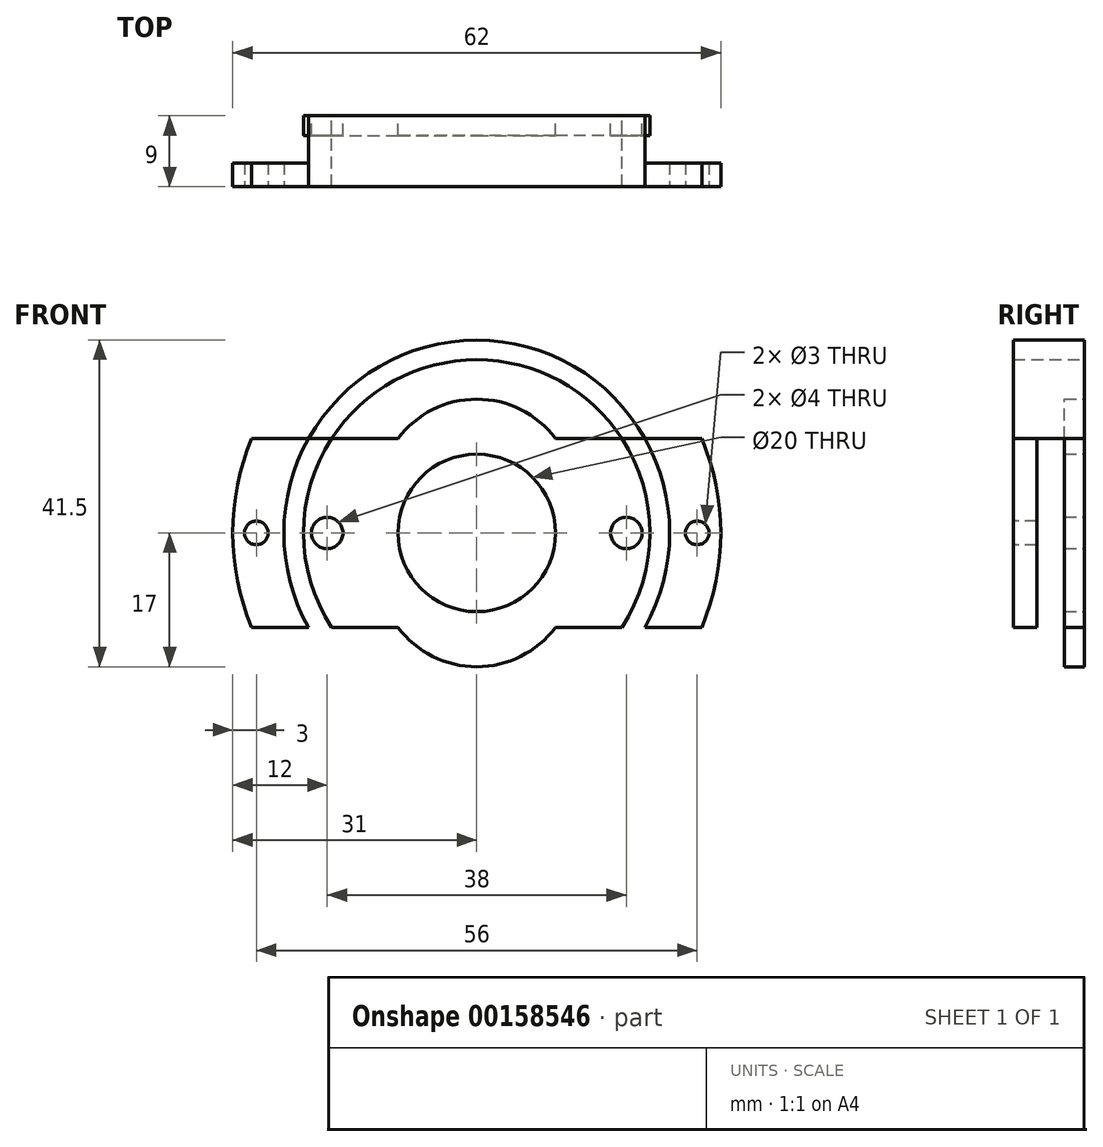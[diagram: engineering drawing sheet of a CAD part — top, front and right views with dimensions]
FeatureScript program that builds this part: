
annotation { "Feature Type Name" : "Feature", "Feature Type Description" : "" }
export const myFeature = defineFeature(function(context is Context, id is Id, definition is map)
    precondition{}
    {
        {
            var Q0;
            Q0=qCreatedBy(makeId("Front.planeOp"),FACE);
            var sketch = newSketch(context, id + "F0", { "sketchPlane" : qUnion([Q0])});
            skCircle(sketch, "E0", {"center": v(0, 0) * mm, "radius": 31 * mm});
            skCircle(sketch, "E1", {"center": v(0, 0) * mm, "radius": 22 * mm});
            skLineSegment(sketch, "E2", {"start": v(-28.58, 12) * mm, "end": v(28.58, 12) * mm});
            skLineSegment(sketch, "E3", {"start": v(28.58, -12) * mm, "end": v(-28.58, -12) * mm});
            skCircle(sketch, "E4", {"center": v(0, 0) * mm, "radius": 24.5 * mm});
            skCircle(sketch, "E5", {"center": v(-28, 0) * mm, "radius": 1.5 * mm});
            skCircle(sketch, "E6", {"center": v(28, 0) * mm, "radius": 1.5 * mm});
            skCircle(sketch, "E7", {"center": v(0, 0) * mm, "radius": 10 * mm});
            skCircle(sketch, "E8", {"center": v(-19, 0) * mm, "radius": 2 * mm});
            skCircle(sketch, "E9", {"center": v(19, 0) * mm, "radius": 2 * mm});
            skArc(sketch, "E10", {"start": v(10, 12) * mm, "mid": v(0, 17) * mm, "end": v(-10, 12) * mm});
            skArc(sketch, "E11", {"start": v(-10, -12) * mm, "mid": v(0, -17) * mm, "end": v(10, -12) * mm});
            skSolve(sketch);
        }
        {
            var Q0;
            Q0=makeQuery(id+"F0.imprint","IMPRINT",FACE,{"disambiguationData":[TD([[makeQuery(id+"F0.imprint","IMPRINT",EDGE,{"derivedFrom":sQuery(id+"F0.wireOp",EDGE,"E7")}),-1.0]])]});
            extrude(context, id + "F1", {"entities" : qUnion([Q0]), "depth" : 2.5 * mm, "offsetDistance" : 25 * mm});
        }
        {
            var Q0;
            {var subQ0=sQuery(id+"F0.wireOp",EDGE,"E2");var subQ1=sQuery(id+"F0.wireOp",EDGE,"E1");var subQ2=makeQuery(id+"F0.imprint","INTERSECT",VERTEX,{"disambiguationData":[OD(0.0)],"derivedFrom":[subQ1,subQ0]});Q0=makeQuery(id+"F0.imprint","IMPRINT",FACE,{"disambiguationData":[TD([[makeQuery(id+"F0.imprint","IMPRINT",EDGE,{"disambiguationData":[TD([[subQ2,-1.0]])],"derivedFrom":subQ1}),-1.0]])]});}
            var Q1;
            {var subQ0=sQuery(id+"F0.wireOp",EDGE,"E2");var subQ1=sQuery(id+"F0.wireOp",EDGE,"E1");var subQ2=makeQuery(id+"F0.imprint","INTERSECT",VERTEX,{"disambiguationData":[OD(1.0)],"derivedFrom":[subQ1,subQ0]});Q1=makeQuery(id+"F0.imprint","IMPRINT",FACE,{"disambiguationData":[TD([[makeQuery(id+"F0.imprint","IMPRINT",EDGE,{"disambiguationData":[TD([[subQ2,1.0]])],"derivedFrom":subQ1}),-1.0]])]});}
            extrude(context, id + "F2", {"entities" : qUnion([Q0, Q1]), "operationType" : NewBodyOperationType.ADD, "depth" : 9 * mm, "offsetDistance" : 25 * mm});
        }
        {
            var Q0;
            {var subQ0=sQuery(id+"F0.wireOp",EDGE,"E4");var subQ1=sQuery(id+"F0.wireOp",EDGE,"E2");var subQ2=makeQuery(id+"F0.imprint","INTERSECT",VERTEX,{"disambiguationData":[OD(0.0)],"derivedFrom":[subQ1,subQ0]});var subQ3=sQuery(id+"F0.wireOp",EDGE,"E3");var subQ5=sQuery(id+"F0.wireOp",EDGE,"E1");var subQ6=makeQuery(id+"F0.imprint","INTERSECT",VERTEX,{"disambiguationData":[OD(0.0)],"derivedFrom":[subQ5,subQ3]});var subQ7=makeQuery(id+"F0.imprint","INTERSECT",VERTEX,{"disambiguationData":[OD(0.0)],"derivedFrom":[subQ5,subQ1]});Q0=makeQuery(id+"F2.opExtrude","CAP_FACE",FACE,{"disambiguationData":[OSD([subQ5,subQ1,subQ3,subQ0]),TDD([makeQuery(id+"F0.imprint","IMPRINT",EDGE,{"disambiguationData":[TD([[subQ7,-1.0]])],"derivedFrom":subQ5}),makeQuery(id+"F0.imprint","IMPRINT",EDGE,{"disambiguationData":[TD([[subQ7,1.0]])],"derivedFrom":subQ1}),makeQuery(id+"F0.imprint","IMPRINT",EDGE,{"disambiguationData":[TD([[subQ6,-1.0]])],"derivedFrom":subQ3}),makeQuery(id+"F0.imprint","IMPRINT",EDGE,{"disambiguationData":[TD([[subQ2,-1.0]])],"derivedFrom":subQ0})])],"isStart":false});}
            var sketch = newSketch(context, id + "F3", { "sketchPlane" : qUnion([Q0])});
            skCircle(sketch, "E12", {"center": v(0, 0) * mm, "radius": 31 * mm});
            skCircle(sketch, "E13", {"center": v(0, 0) * mm, "radius": 22 * mm});
            skLineSegment(sketch, "E14", {"start": v(-28.58, 12) * mm, "end": v(28.58, 12) * mm});
            skLineSegment(sketch, "E15", {"start": v(28.58, -12) * mm, "end": v(-28.58, -12) * mm});
            skCircle(sketch, "E16", {"center": v(0, 0) * mm, "radius": 24.5 * mm});
            skCircle(sketch, "E17", {"center": v(-28, 0) * mm, "radius": 1.5 * mm});
            skCircle(sketch, "E18", {"center": v(28, 0) * mm, "radius": 1.5 * mm});
            skCircle(sketch, "E19", {"center": v(0, 0) * mm, "radius": 15 * mm});
            skSolve(sketch);
        }
        {
            var Q0;
            Q0=makeQuery(id+"F3.imprint","IMPRINT",FACE,{"disambiguationData":[TD([[makeQuery(id+"F3.imprint","IMPRINT",EDGE,{"derivedFrom":sQuery(id+"F3.wireOp",EDGE,"E17")}),-1.0]])]});
            var Q1;
            Q1=makeQuery(id+"F3.imprint","IMPRINT",FACE,{"disambiguationData":[TD([[makeQuery(id+"F3.imprint","IMPRINT",EDGE,{"derivedFrom":sQuery(id+"F3.wireOp",EDGE,"E18")}),-1.0]])]});
            extrude(context, id + "F4", {"entities" : qUnion([Q0, Q1]), "operationType" : NewBodyOperationType.ADD, "oppositeDirection" : true, "depth" : 3 * mm, "offsetDistance" : 25 * mm});
        }
        {
            var Q0;
            {var subQ0=sQuery(id+"F0.wireOp",EDGE,"E10");Q0=makeQuery(id+"F0.imprint","IMPRINT",FACE,{"disambiguationData":[TD([[makeQuery(id+"F0.imprint","IMPRINT",EDGE,{"derivedFrom":subQ0}),1.0]])]});}
            var Q1;
            {var subQ0=sQuery(id+"F0.wireOp",EDGE,"E11");Q1=makeQuery(id+"F0.imprint","IMPRINT",FACE,{"disambiguationData":[TD([[makeQuery(id+"F0.imprint","IMPRINT",EDGE,{"derivedFrom":subQ0}),1.0]])]});}
            extrude(context, id + "F5", {"entities" : qUnion([Q0, Q1]), "operationType" : NewBodyOperationType.ADD, "depth" : 2.5 * mm, "offsetDistance" : 25 * mm});
        }
    });
